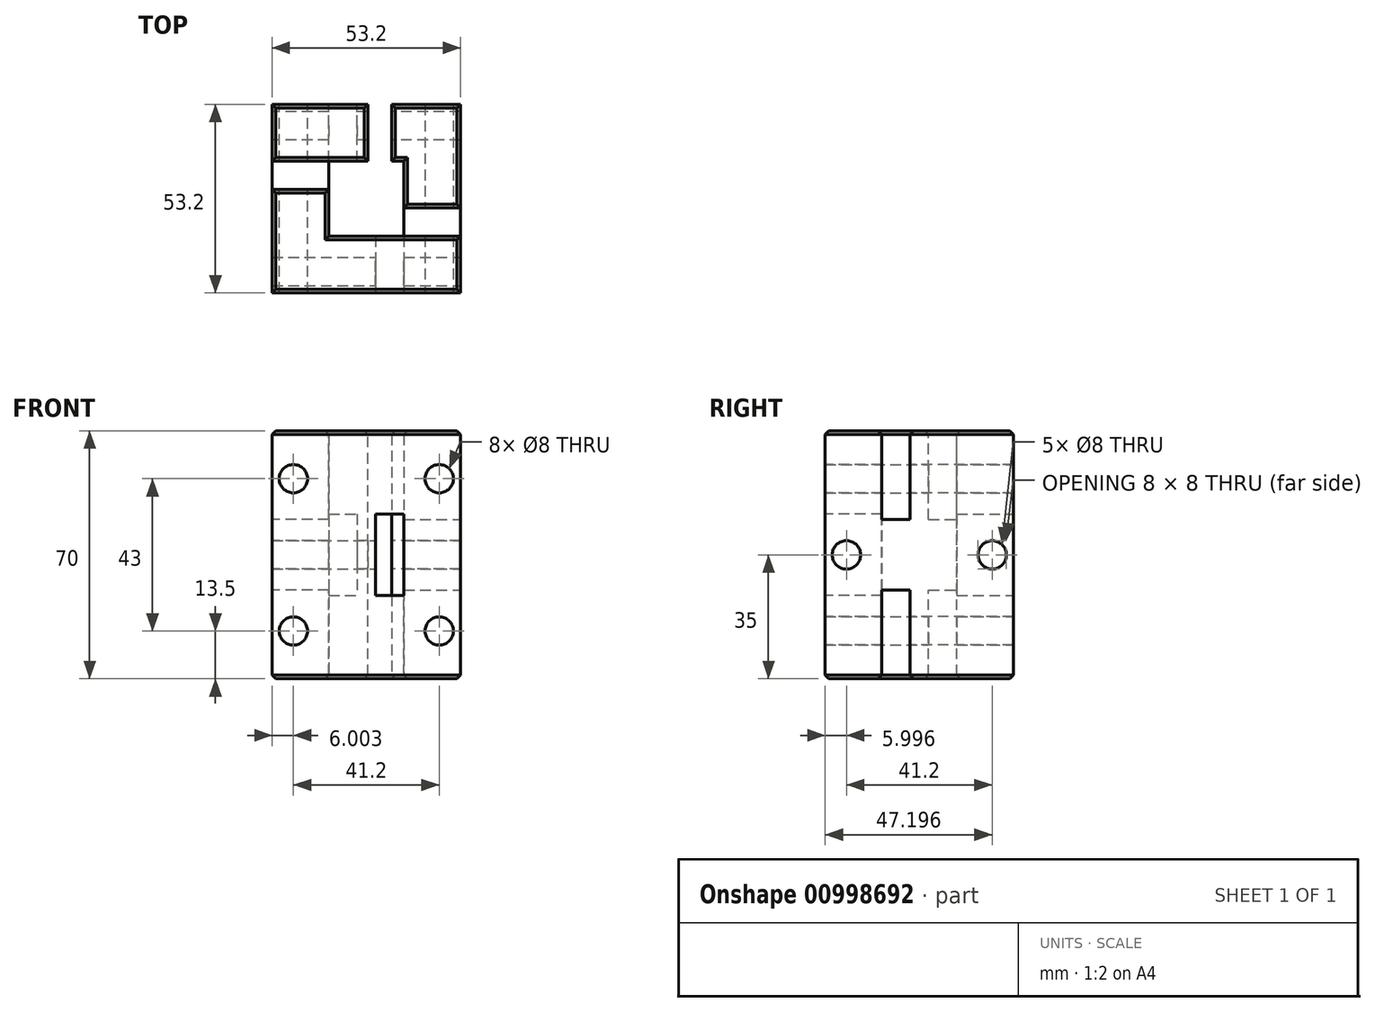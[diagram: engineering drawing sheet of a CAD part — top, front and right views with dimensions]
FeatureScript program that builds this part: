
annotation { "Feature Type Name" : "Feature", "Feature Type Description" : "" }
export const myFeature = defineFeature(function(context is Context, id is Id, definition is map)
    precondition{}
    {
        {
            var Q0;
            Q0=qCreatedBy(makeId("Top.planeOp"),FACE);
            var sketch = newSketch(context, id + "F0", { "sketchPlane" : qUnion([Q0])});
            skLineSegment(sketch, "E0.bottom", {"start": v(-39.95, 37.27) * mm, "end": v(-18.75, 37.27) * mm});
            skLineSegment(sketch, "E0.top", {"start": v(-39.95, 16.07) * mm, "end": v(-18.75, 16.07) * mm});
            skLineSegment(sketch, "E0.left", {"start": v(-39.95, 37.27) * mm, "end": v(-39.95, 16.07) * mm});
            skLineSegment(sketch, "E0.right", {"start": v(-18.75, 37.27) * mm, "end": v(-18.75, 16.07) * mm});
            skLineSegment(sketch, "E1.0", {"start": v(-55.95, 53.27) * mm, "end": v(-2.75, 53.27) * mm});
            skLineSegment(sketch, "E1.1", {"start": v(-55.95, 53.27) * mm, "end": v(-55.95, 0.07) * mm});
            skLineSegment(sketch, "E1.2", {"start": v(-55.95, 0.07) * mm, "end": v(-2.75, 0.07) * mm});
            skLineSegment(sketch, "E1.3", {"start": v(-2.75, 53.27) * mm, "end": v(-2.75, 0.07) * mm});
            skSolve(sketch);
        }
        {
            var Q0;
            Q0=makeQuery(id+"F0.imprint","IMPRINT",FACE,{"disambiguationData":[TD([[makeQuery(id+"F0.imprint","IMPRINT",EDGE,{"derivedFrom":sQuery(id+"F0.wireOp",EDGE,"E0.bottom")}),1.0]])]});
            extrude(context, id + "F1", {"entities" : qUnion([Q0]), "depth" : 70 * mm, "offsetDistance" : 25 * mm});
        }
        {
            var Q0;
            Q0=makeQuery(id+"F1.opExtrude","SWEPT_FACE",FACE,{"disambiguationData":[OSD([sQuery(id+"F0.wireOp",EDGE,"E1.1")])]});
            var sketch = newSketch(context, id + "F2", { "sketchPlane" : qUnion([Q0])});
            skLineSegment(sketch, "E2.bottom", {"start": v(-53.27, 0) * mm, "end": v(-37.27, 0) * mm});
            skLineSegment(sketch, "E2.top", {"start": v(-53.27, 70) * mm, "end": v(-37.27, 70) * mm});
            skLineSegment(sketch, "E2.left", {"start": v(-53.27, 0) * mm, "end": v(-53.27, 70) * mm});
            skLineSegment(sketch, "E2.right", {"start": v(-37.27, 0) * mm, "end": v(-37.27, 70) * mm});
            skLineSegment(sketch, "E3.bottom", {"start": v(-37.27, 2) * mm, "end": v(-29.27, 2) * mm});
            skLineSegment(sketch, "E3.top", {"start": v(-37.27, 25) * mm, "end": v(-29.27, 25) * mm});
            skLineSegment(sketch, "E3.left", {"start": v(-37.27, 2) * mm, "end": v(-37.27, 25) * mm});
            skLineSegment(sketch, "E3.right", {"start": v(-29.27, 2) * mm, "end": v(-29.27, 25) * mm});
            skLineSegment(sketch, "E4.bottom", {"start": v(-37.27, 68) * mm, "end": v(-29.27, 68) * mm});
            skLineSegment(sketch, "E4.top", {"start": v(-37.27, 45) * mm, "end": v(-29.27, 45) * mm});
            skLineSegment(sketch, "E4.left", {"start": v(-37.27, 68) * mm, "end": v(-37.27, 45) * mm});
            skLineSegment(sketch, "E4.right", {"start": v(-29.27, 68) * mm, "end": v(-29.27, 45) * mm});
            skPoint(sketch, "E5.centerSnap0", {"position": v(-53.27, 35) * mm});
            skPoint(sketch, "E6.oppositeSnap0", {"position": v(-26.67, 0) * mm});
            skLineSegment(sketch, "E6.top", {"start": v(-37.27, 0) * mm, "end": v(-29.27, 0) * mm});
            skLineSegment(sketch, "E6.left", {"start": v(-37.27, 2) * mm, "end": v(-37.27, 0) * mm});
            skLineSegment(sketch, "E6.right", {"start": v(-29.27, 2) * mm, "end": v(-29.27, 0) * mm});
            skLineSegment(sketch, "E7.bottom", {"start": v(-29.27, 68) * mm, "end": v(-37.27, 68) * mm});
            skLineSegment(sketch, "E7.top", {"start": v(-29.27, 70) * mm, "end": v(-37.27, 70) * mm});
            skLineSegment(sketch, "E7.left", {"start": v(-29.27, 68) * mm, "end": v(-29.27, 70) * mm});
            skLineSegment(sketch, "E7.right", {"start": v(-37.27, 68) * mm, "end": v(-37.27, 70) * mm});
            skCircle(sketch, "E8", {"center": v(-47.27, 35) * mm, "radius": 4 * mm});
            skLineSegment(sketch, "E9.bottom", {"start": v(-29.27, 17.5) * mm, "end": v(-37.27, 17.5) * mm});
            skLineSegment(sketch, "E9.top", {"start": v(-29.27, 9.5) * mm, "end": v(-37.27, 9.5) * mm});
            skLineSegment(sketch, "E9.left", {"start": v(-29.27, 17.5) * mm, "end": v(-29.27, 9.5) * mm});
            skLineSegment(sketch, "E9.right", {"start": v(-37.27, 17.5) * mm, "end": v(-37.27, 9.5) * mm});
            skPoint(sketch, "E9.middle", {"position": v(-33.27, 13.5) * mm});
            skPoint(sketch, "E9.middle.positionSnap0", {"position": v(-33.27, 25) * mm});
            skPoint(sketch, "E9.middle.positionSnap1", {"position": v(-37.27, 13.5) * mm});
            skPoint(sketch, "E9.centerSnap0", {"position": v(-33.27, 25) * mm});
            skPoint(sketch, "E9.centerSnap1", {"position": v(-37.27, 13.5) * mm});
            skLineSegment(sketch, "E10.bottom", {"start": v(-29.27, 17.5) * mm, "end": v(-53.27, 17.5) * mm});
            skLineSegment(sketch, "E10.top", {"start": v(-29.27, 9.5) * mm, "end": v(-53.27, 9.5) * mm});
            skLineSegment(sketch, "E10.right", {"start": v(-53.27, 17.5) * mm, "end": v(-53.27, 9.5) * mm});
            skLineSegment(sketch, "E11.bottom", {"start": v(-29.27, 60.5) * mm, "end": v(-37.27, 60.5) * mm});
            skLineSegment(sketch, "E11.top", {"start": v(-29.27, 52.5) * mm, "end": v(-37.27, 52.5) * mm});
            skLineSegment(sketch, "E11.left", {"start": v(-29.27, 60.5) * mm, "end": v(-29.27, 52.5) * mm});
            skLineSegment(sketch, "E11.right", {"start": v(-37.27, 60.5) * mm, "end": v(-37.27, 52.5) * mm});
            skPoint(sketch, "E11.middle", {"position": v(-33.27, 56.5) * mm});
            skPoint(sketch, "E11.middle.positionSnap0", {"position": v(-33.27, 45) * mm});
            skPoint(sketch, "E11.middle.positionSnap1", {"position": v(-37.27, 56.5) * mm});
            skPoint(sketch, "E11.centerSnap0", {"position": v(-33.27, 45) * mm});
            skPoint(sketch, "E11.centerSnap1", {"position": v(-37.27, 56.5) * mm});
            skLineSegment(sketch, "E12.bottom", {"start": v(-29.27, 52.5) * mm, "end": v(-53.27, 52.5) * mm});
            skLineSegment(sketch, "E12.top", {"start": v(-29.27, 60.5) * mm, "end": v(-53.27, 60.5) * mm});
            skLineSegment(sketch, "E12.left", {"start": v(-29.27, 52.5) * mm, "end": v(-29.27, 60.5) * mm});
            skLineSegment(sketch, "E12.right", {"start": v(-53.27, 52.5) * mm, "end": v(-53.27, 60.5) * mm});
            skSolve(sketch);
        }
        {
            var Q0;
            Q0=makeQuery(id+"F1.opExtrude","SWEPT_FACE",FACE,{"disambiguationData":[OSD([sQuery(id+"F0.wireOp",EDGE,"E1.0")])]});
            var sketch = newSketch(context, id + "F3", { "sketchPlane" : qUnion([Q0])});
            skLineSegment(sketch, "E13.bottom", {"start": v(55.95, 70) * mm, "end": v(39.95, 70) * mm});
            skLineSegment(sketch, "E13.top", {"start": v(55.95, 0) * mm, "end": v(39.95, 0) * mm});
            skLineSegment(sketch, "E13.left", {"start": v(55.95, 70) * mm, "end": v(55.95, 0) * mm});
            skLineSegment(sketch, "E13.right", {"start": v(39.95, 70) * mm, "end": v(39.95, 0) * mm});
            skLineSegment(sketch, "E14.bottom", {"start": v(39.95, 46.5) * mm, "end": v(31.95, 46.5) * mm});
            skLineSegment(sketch, "E14.top", {"start": v(39.95, 23.5) * mm, "end": v(31.95, 23.5) * mm});
            skLineSegment(sketch, "E14.left", {"start": v(39.95, 46.5) * mm, "end": v(39.95, 23.5) * mm});
            skLineSegment(sketch, "E14.right", {"start": v(31.95, 46.5) * mm, "end": v(31.95, 23.5) * mm});
            skPoint(sketch, "E15", {"position": v(39.95, 35) * mm});
            skCircle(sketch, "E16", {"center": v(49.95, 56.5) * mm, "radius": 4 * mm});
            skCircle(sketch, "E17", {"center": v(49.95, 13.5) * mm, "radius": 4 * mm});
            skSolve(sketch);
        }
        {
            var Q0;
            {var subQ0=sQuery(id+"F2.wireOp",EDGE,"E4.top");Q0=makeQuery(id+"F2.imprint","IMPRINT",FACE,{"disambiguationData":[TD([[makeQuery(id+"F2.imprint","IMPRINT",EDGE,{"derivedFrom":subQ0}),1.0]])]});}
            var Q1;
            {var subQ0=sQuery(id+"F2.wireOp",EDGE,"E11.bottom");Q1=makeQuery(id+"F2.imprint","IMPRINT",FACE,{"disambiguationData":[TD([[makeQuery(id+"F2.imprint","IMPRINT",EDGE,{"derivedFrom":subQ0}),1.0]])]});}
            var Q2;
            {var subQ0=sQuery(id+"F2.wireOp",EDGE,"E4.bottom");Q2=makeQuery(id+"F2.imprint","IMPRINT",FACE,{"disambiguationData":[TD([[makeQuery(id+"F2.imprint","IMPRINT",EDGE,{"derivedFrom":subQ0}),-1.0]])]});}
            var Q3;
            {var subQ2=sQuery(id+"F2.wireOp",EDGE,"E4.bottom");Q3=makeQuery(id+"F2.imprint","IMPRINT",FACE,{"disambiguationData":[TD([[makeQuery(id+"F2.imprint","IMPRINT",EDGE,{"derivedFrom":subQ2}),1.0]])]});}
            var Q4;
            {var subQ2=sQuery(id+"F2.wireOp",EDGE,"E3.bottom");Q4=makeQuery(id+"F2.imprint","IMPRINT",FACE,{"disambiguationData":[TD([[makeQuery(id+"F2.imprint","IMPRINT",EDGE,{"derivedFrom":subQ2}),-1.0]])]});}
            var Q5;
            {var subQ0=sQuery(id+"F2.wireOp",EDGE,"E3.bottom");Q5=makeQuery(id+"F2.imprint","IMPRINT",FACE,{"disambiguationData":[TD([[makeQuery(id+"F2.imprint","IMPRINT",EDGE,{"derivedFrom":subQ0}),1.0]])]});}
            var Q6;
            {var subQ0=sQuery(id+"F2.wireOp",EDGE,"E9.bottom");Q6=makeQuery(id+"F2.imprint","IMPRINT",FACE,{"disambiguationData":[TD([[makeQuery(id+"F2.imprint","IMPRINT",EDGE,{"derivedFrom":subQ0}),1.0]])]});}
            var Q7;
            {var subQ0=sQuery(id+"F2.wireOp",EDGE,"E3.top");Q7=makeQuery(id+"F2.imprint","IMPRINT",FACE,{"disambiguationData":[TD([[makeQuery(id+"F2.imprint","IMPRINT",EDGE,{"derivedFrom":subQ0}),-1.0]])]});}
            extrude(context, id + "F4", {"entities" : qUnion([Q0, Q1, Q2, Q3, Q4, Q5, Q6, Q7]), "operationType" : NewBodyOperationType.REMOVE, "oppositeDirection" : true, "depth" : 24 * mm, "offsetDistance" : 25 * mm});
        }
        {
            var Q0;
            {var subQ2=sQuery(id+"F3.wireOp",EDGE,"E14.bottom");Q0=makeQuery(id+"F3.imprint","IMPRINT",FACE,{"disambiguationData":[TD([[makeQuery(id+"F3.imprint","IMPRINT",EDGE,{"derivedFrom":subQ2}),1.0]])]});}
            extrude(context, id + "F5", {"entities" : qUnion([Q0]), "operationType" : NewBodyOperationType.REMOVE, "oppositeDirection" : true, "depth" : 25 * mm, "offsetDistance" : 25 * mm});
        }
        {
            var Q0;
            Q0=makeQuery(id+"F2.imprint","IMPRINT",FACE,{"disambiguationData":[TD([[makeQuery(id+"F2.imprint","IMPRINT",EDGE,{"derivedFrom":sQuery(id+"F2.wireOp",EDGE,"E8")}),1.0]])]});
            extrude(context, id + "F6", {"entities" : qUnion([Q0]), "operationType" : NewBodyOperationType.REMOVE, "oppositeDirection" : true, "depth" : 90 * mm, "offsetDistance" : 25 * mm});
        }
        {
            var Q0;
            Q0=makeQuery(id+"F1.opExtrude","SWEPT_FACE",FACE,{"disambiguationData":[OSD([sQuery(id+"F0.wireOp",EDGE,"E1.3")])]});
            var sketch = newSketch(context, id + "F7", { "sketchPlane" : qUnion([Q0])});
            skLineSegment(sketch, "E18.bottom", {"start": v(0.07, 0) * mm, "end": v(16.07, 0) * mm});
            skLineSegment(sketch, "E18.top", {"start": v(0.07, 70) * mm, "end": v(16.07, 70) * mm});
            skLineSegment(sketch, "E18.left", {"start": v(0.07, 0) * mm, "end": v(0.07, 70) * mm});
            skLineSegment(sketch, "E18.right", {"start": v(16.07, 0) * mm, "end": v(16.07, 70) * mm});
            skLineSegment(sketch, "E19.bottom", {"start": v(16.07, 2) * mm, "end": v(24.07, 2) * mm});
            skLineSegment(sketch, "E19.top", {"start": v(16.07, 25) * mm, "end": v(24.07, 25) * mm});
            skLineSegment(sketch, "E19.left", {"start": v(16.07, 2) * mm, "end": v(16.07, 25) * mm});
            skLineSegment(sketch, "E19.right", {"start": v(24.07, 2) * mm, "end": v(24.07, 25) * mm});
            skLineSegment(sketch, "E20.bottom", {"start": v(16.07, 68) * mm, "end": v(24.07, 68) * mm});
            skLineSegment(sketch, "E20.top", {"start": v(16.07, 45) * mm, "end": v(24.07, 45) * mm});
            skLineSegment(sketch, "E20.left", {"start": v(16.07, 68) * mm, "end": v(16.07, 45) * mm});
            skLineSegment(sketch, "E20.right", {"start": v(24.07, 68) * mm, "end": v(24.07, 45) * mm});
            skLineSegment(sketch, "E21.bottom", {"start": v(24.07, 68) * mm, "end": v(16.07, 68) * mm});
            skLineSegment(sketch, "E21.top", {"start": v(24.07, 70) * mm, "end": v(16.07, 70) * mm});
            skLineSegment(sketch, "E21.left", {"start": v(24.07, 68) * mm, "end": v(24.07, 70) * mm});
            skLineSegment(sketch, "E21.right", {"start": v(16.07, 68) * mm, "end": v(16.07, 70) * mm});
            skLineSegment(sketch, "E22.bottom", {"start": v(24.07, 2) * mm, "end": v(16.07, 2) * mm});
            skLineSegment(sketch, "E22.top", {"start": v(24.07, 0) * mm, "end": v(16.07, 0) * mm});
            skLineSegment(sketch, "E22.left", {"start": v(24.07, 2) * mm, "end": v(24.07, 0) * mm});
            skLineSegment(sketch, "E22.right", {"start": v(16.07, 2) * mm, "end": v(16.07, 0) * mm});
            skCircle(sketch, "E23", {"center": v(6.07, 35) * mm, "radius": 4 * mm});
            skPoint(sketch, "E23.centerSnap0", {"position": v(0.07, 35) * mm});
            skLineSegment(sketch, "E24.bottom", {"start": v(24.07, 17.5) * mm, "end": v(16.07, 17.5) * mm});
            skLineSegment(sketch, "E24.top", {"start": v(24.07, 9.5) * mm, "end": v(16.07, 9.5) * mm});
            skLineSegment(sketch, "E24.left", {"start": v(24.07, 17.5) * mm, "end": v(24.07, 9.5) * mm});
            skLineSegment(sketch, "E24.right", {"start": v(16.07, 17.5) * mm, "end": v(16.07, 9.5) * mm});
            skPoint(sketch, "E24.middle", {"position": v(20.07, 13.5) * mm});
            skPoint(sketch, "E24.middle.positionSnap0", {"position": v(16.07, 13.5) * mm});
            skPoint(sketch, "E24.middle.positionSnap1", {"position": v(20.07, 25) * mm});
            skPoint(sketch, "E24.centerSnap0", {"position": v(16.07, 13.5) * mm});
            skPoint(sketch, "E24.centerSnap1", {"position": v(20.07, 25) * mm});
            skLineSegment(sketch, "E25.bottom", {"start": v(24.07, 60.5) * mm, "end": v(16.07, 60.5) * mm});
            skLineSegment(sketch, "E25.top", {"start": v(24.07, 52.5) * mm, "end": v(16.07, 52.5) * mm});
            skLineSegment(sketch, "E25.left", {"start": v(24.07, 60.5) * mm, "end": v(24.07, 52.5) * mm});
            skLineSegment(sketch, "E25.right", {"start": v(16.07, 60.5) * mm, "end": v(16.07, 52.5) * mm});
            skPoint(sketch, "E25.middle", {"position": v(20.07, 56.5) * mm});
            skPoint(sketch, "E25.middle.positionSnap0", {"position": v(16.07, 56.5) * mm});
            skPoint(sketch, "E25.middle.positionSnap1", {"position": v(20.07, 45) * mm});
            skPoint(sketch, "E25.centerSnap0", {"position": v(16.07, 56.5) * mm});
            skPoint(sketch, "E25.centerSnap1", {"position": v(20.07, 45) * mm});
            skLineSegment(sketch, "E26.bottom", {"start": v(24.07, 52.5) * mm, "end": v(0.07, 52.5) * mm});
            skLineSegment(sketch, "E26.top", {"start": v(24.07, 60.5) * mm, "end": v(0.07, 60.5) * mm});
            skLineSegment(sketch, "E26.left", {"start": v(24.07, 52.5) * mm, "end": v(24.07, 60.5) * mm});
            skLineSegment(sketch, "E26.right", {"start": v(0.07, 52.5) * mm, "end": v(0.07, 60.5) * mm});
            skLineSegment(sketch, "E27.bottom", {"start": v(24.07, 9.5) * mm, "end": v(0.07, 9.5) * mm});
            skLineSegment(sketch, "E27.top", {"start": v(24.07, 17.5) * mm, "end": v(0.07, 17.5) * mm});
            skLineSegment(sketch, "E27.left", {"start": v(24.07, 9.5) * mm, "end": v(24.07, 17.5) * mm});
            skLineSegment(sketch, "E27.right", {"start": v(0.07, 9.5) * mm, "end": v(0.07, 17.5) * mm});
            skSolve(sketch);
        }
        {
            var Q0;
            {var subQ0=sQuery(id+"F7.wireOp",EDGE,"E20.top");Q0=makeQuery(id+"F7.imprint","IMPRINT",FACE,{"disambiguationData":[TD([[makeQuery(id+"F7.imprint","IMPRINT",EDGE,{"derivedFrom":subQ0}),1.0]])]});}
            var Q1;
            {var subQ2=sQuery(id+"F7.wireOp",EDGE,"E20.bottom");Q1=makeQuery(id+"F7.imprint","IMPRINT",FACE,{"disambiguationData":[TD([[makeQuery(id+"F7.imprint","IMPRINT",EDGE,{"derivedFrom":subQ2}),1.0]])]});}
            var Q2;
            {var subQ0=sQuery(id+"F7.wireOp",EDGE,"E19.top");Q2=makeQuery(id+"F7.imprint","IMPRINT",FACE,{"disambiguationData":[TD([[makeQuery(id+"F7.imprint","IMPRINT",EDGE,{"derivedFrom":subQ0}),-1.0]])]});}
            var Q3;
            {var subQ2=sQuery(id+"F7.wireOp",EDGE,"E19.bottom");Q3=makeQuery(id+"F7.imprint","IMPRINT",FACE,{"disambiguationData":[TD([[makeQuery(id+"F7.imprint","IMPRINT",EDGE,{"derivedFrom":subQ2}),-1.0]])]});}
            var Q4;
            {var subQ0=sQuery(id+"F7.wireOp",EDGE,"E25.bottom");Q4=makeQuery(id+"F7.imprint","IMPRINT",FACE,{"disambiguationData":[TD([[makeQuery(id+"F7.imprint","IMPRINT",EDGE,{"derivedFrom":subQ0}),1.0]])]});}
            var Q5;
            {var subQ0=sQuery(id+"F7.wireOp",EDGE,"E20.bottom");Q5=makeQuery(id+"F7.imprint","IMPRINT",FACE,{"disambiguationData":[TD([[makeQuery(id+"F7.imprint","IMPRINT",EDGE,{"derivedFrom":subQ0}),-1.0]])]});}
            var Q6;
            {var subQ0=sQuery(id+"F7.wireOp",EDGE,"E24.bottom");Q6=makeQuery(id+"F7.imprint","IMPRINT",FACE,{"disambiguationData":[TD([[makeQuery(id+"F7.imprint","IMPRINT",EDGE,{"derivedFrom":subQ0}),1.0]])]});}
            var Q7;
            {var subQ0=sQuery(id+"F7.wireOp",EDGE,"E19.bottom");Q7=makeQuery(id+"F7.imprint","IMPRINT",FACE,{"disambiguationData":[TD([[makeQuery(id+"F7.imprint","IMPRINT",EDGE,{"derivedFrom":subQ0}),1.0]])]});}
            extrude(context, id + "F8", {"entities" : qUnion([Q0, Q1, Q2, Q3, Q4, Q5, Q6, Q7]), "operationType" : NewBodyOperationType.REMOVE, "oppositeDirection" : true, "depth" : 25 * mm, "offsetDistance" : 25 * mm});
        }
        {
            var Q0;
            Q0=makeQuery(id+"F3.imprint","IMPRINT",FACE,{"disambiguationData":[TD([[makeQuery(id+"F3.imprint","IMPRINT",EDGE,{"derivedFrom":sQuery(id+"F3.wireOp",EDGE,"E16")}),1.0]])]});
            var Q1;
            Q1=makeQuery(id+"F3.imprint","IMPRINT",FACE,{"disambiguationData":[TD([[makeQuery(id+"F3.imprint","IMPRINT",EDGE,{"derivedFrom":sQuery(id+"F3.wireOp",EDGE,"E17")}),1.0]])]});
            extrude(context, id + "F9", {"entities" : qUnion([Q0, Q1]), "operationType" : NewBodyOperationType.REMOVE, "oppositeDirection" : true, "depth" : 100 * mm, "offsetDistance" : 25 * mm});
        }
        {
            var Q0;
            Q0=makeQuery(id+"F7.imprint","IMPRINT",FACE,{"disambiguationData":[TD([[makeQuery(id+"F7.imprint","IMPRINT",EDGE,{"derivedFrom":sQuery(id+"F7.wireOp",EDGE,"E23")}),1.0]])]});
            extrude(context, id + "F10", {"entities" : qUnion([Q0]), "operationType" : NewBodyOperationType.REMOVE, "oppositeDirection" : true, "depth" : 90 * mm, "offsetDistance" : 25 * mm});
        }
        {
            var Q0;
            Q0=makeQuery(id+"F1.opExtrude","SWEPT_FACE",FACE,{"disambiguationData":[OSD([sQuery(id+"F0.wireOp",EDGE,"E1.2")])]});
            var sketch = newSketch(context, id + "F11", { "sketchPlane" : qUnion([Q0])});
            skLineSegment(sketch, "E28.bottom", {"start": v(-2.75, 70) * mm, "end": v(-18.75, 70) * mm});
            skLineSegment(sketch, "E28.top", {"start": v(-2.75, 0) * mm, "end": v(-18.75, 0) * mm});
            skLineSegment(sketch, "E28.left", {"start": v(-2.75, 70) * mm, "end": v(-2.75, 0) * mm});
            skLineSegment(sketch, "E28.right", {"start": v(-18.75, 70) * mm, "end": v(-18.75, 0) * mm});
            skLineSegment(sketch, "E29.bottom", {"start": v(-18.75, 46.5) * mm, "end": v(-26.75, 46.5) * mm});
            skLineSegment(sketch, "E29.top", {"start": v(-18.75, 23.5) * mm, "end": v(-26.75, 23.5) * mm});
            skLineSegment(sketch, "E29.left", {"start": v(-18.75, 46.5) * mm, "end": v(-18.75, 23.5) * mm});
            skLineSegment(sketch, "E29.right", {"start": v(-26.75, 46.5) * mm, "end": v(-26.75, 23.5) * mm});
            skPoint(sketch, "E30", {"position": v(-18.75, 35) * mm});
            skCircle(sketch, "E31", {"center": v(-8.75, 56.5) * mm, "radius": 4 * mm});
            skCircle(sketch, "E32", {"center": v(-8.75, 13.5) * mm, "radius": 4 * mm});
            skSolve(sketch);
        }
        {
            var Q0;
            {var subQ2=sQuery(id+"F11.wireOp",EDGE,"E29.bottom");Q0=makeQuery(id+"F11.imprint","IMPRINT",FACE,{"disambiguationData":[TD([[makeQuery(id+"F11.imprint","IMPRINT",EDGE,{"derivedFrom":subQ2}),1.0]])]});}
            extrude(context, id + "F12", {"entities" : qUnion([Q0]), "operationType" : NewBodyOperationType.REMOVE, "oppositeDirection" : true, "depth" : 25 * mm, "offsetDistance" : 25 * mm});
        }
        {
            var Q0;
            Q0=makeQuery(id+"F11.imprint","IMPRINT",FACE,{"disambiguationData":[TD([[makeQuery(id+"F11.imprint","IMPRINT",EDGE,{"derivedFrom":sQuery(id+"F11.wireOp",EDGE,"E32")}),1.0]])]});
            var Q1;
            Q1=makeQuery(id+"F11.imprint","IMPRINT",FACE,{"disambiguationData":[TD([[makeQuery(id+"F11.imprint","IMPRINT",EDGE,{"derivedFrom":sQuery(id+"F11.wireOp",EDGE,"E31")}),1.0]])]});
            extrude(context, id + "F13", {"entities" : qUnion([Q0, Q1]), "operationType" : NewBodyOperationType.REMOVE, "oppositeDirection" : true, "depth" : 90 * mm, "offsetDistance" : 25 * mm});
        }
        {
            var Q0;
            Q0=makeQuery(id+"F1.opExtrude","SWEPT_FACE",FACE,{"disambiguationData":[OSD([sQuery(id+"F0.wireOp",EDGE,"E1.0")])]});
            var sketch = newSketch(context, id + "F14", { "sketchPlane" : qUnion([Q0])});
            skLineSegment(sketch, "E33", {"start": v(1.95, 70) * mm, "end": v(15.45, 70) * mm});
            skLineSegment(sketch, "E34", {"start": v(28.95, 70) * mm, "end": v(42.45, 70) * mm});
            skLineSegment(sketch, "E35", {"start": v(15.45, 70) * mm, "end": v(28.95, 70) * mm});
            skLineSegment(sketch, "E36", {"start": v(42.45, 70) * mm, "end": v(55.95, 70) * mm});
            skLineSegment(sketch, "E37", {"start": v(1.95, 70) * mm, "end": v(1.95, 52.5) * mm});
            skLineSegment(sketch, "E38", {"start": v(1.95, 0) * mm, "end": v(15.45, 0) * mm});
            skLineSegment(sketch, "E39", {"start": v(28.95, 0) * mm, "end": v(42.45, 0) * mm});
            skLineSegment(sketch, "E40", {"start": v(15.45, 0) * mm, "end": v(28.95, 0) * mm});
            skLineSegment(sketch, "E41", {"start": v(42.45, 0) * mm, "end": v(55.95, 0) * mm});
            skLineSegment(sketch, "E42", {"start": v(1.95, 35) * mm, "end": v(1.95, 17.5) * mm});
            skLineSegment(sketch, "E43", {"start": v(1.95, 52.5) * mm, "end": v(1.95, 35) * mm});
            skLineSegment(sketch, "E44", {"start": v(1.95, 17.5) * mm, "end": v(1.95, 0) * mm});
            skLineSegment(sketch, "E45", {"start": v(1.95, 52.5) * mm, "end": v(55.95, 52.5) * mm});
            skLineSegment(sketch, "E46", {"start": v(55.95, 52.5) * mm, "end": v(55.95, 17.5) * mm});
            skLineSegment(sketch, "E47", {"start": v(55.95, 17.5) * mm, "end": v(1.95, 17.5) * mm});
            skPoint(sketch, "E48.endSnap0", {"position": v(22.2, 70) * mm});
            skLineSegment(sketch, "E49", {"start": v(28.95, 70) * mm, "end": v(22.2, 52.5) * mm});
            skLineSegment(sketch, "E50", {"start": v(22.2, 52.5) * mm, "end": v(22.2, 70) * mm});
            skLineSegment(sketch, "E51", {"start": v(28.95, 0) * mm, "end": v(22.2, 17.5) * mm});
            skPoint(sketch, "E51.endSnap0", {"position": v(22.2, 0) * mm});
            skLineSegment(sketch, "E52", {"start": v(22.2, 17.5) * mm, "end": v(22.2, 0) * mm});
            skPoint(sketch, "E53.startSnap0", {"position": v(25.57, 61.25) * mm});
            skLineSegment(sketch, "E54", {"start": v(22.2, 47) * mm, "end": v(28.95, 61.25) * mm});
            skPoint(sketch, "E55.startSnap0", {"position": v(22.2, 8.75) * mm});
            skLineSegment(sketch, "E56", {"start": v(22.2, 23) * mm, "end": v(28.95, 8.75) * mm});
            skLineSegment(sketch, "E57", {"start": v(28.95, 8.75) * mm, "end": v(28.95, 61.25) * mm});
            skPoint(sketch, "E58.endSnap0", {"position": v(28.95, 35) * mm});
            skPoint(sketch, "E59", {"position": v(22.2, 24.5) * mm});
            skPoint(sketch, "E60", {"position": v(22.2, 45.5) * mm});
            skPoint(sketch, "E61", {"position": v(27.45, 35) * mm});
            skLineSegment(sketch, "E62", {"start": v(27.45, 35) * mm, "end": v(22.2, 45.5) * mm});
            skLineSegment(sketch, "E63", {"start": v(22.2, 24.5) * mm, "end": v(27.45, 35) * mm});
            skLineSegment(sketch, "E64", {"start": v(22.2, 45.5) * mm, "end": v(22.2, 24.5) * mm});
            skLineSegment(sketch, "E65", {"start": v(28.95, 33.5) * mm, "end": v(28.95, 36.5) * mm});
            skLineSegment(sketch, "E66", {"start": v(28.95, 36.5) * mm, "end": v(22.2, 47) * mm});
            skLineSegment(sketch, "E67", {"start": v(28.95, 33.5) * mm, "end": v(22.2, 23) * mm});
            skLineSegment(sketch, "E68", {"start": v(28.95, 70) * mm, "end": v(28.95, 0) * mm});
            skLineSegment(sketch, "E69", {"start": v(22.2, 0) * mm, "end": v(22.2, 70) * mm});
            skSolve(sketch);
        }
        {
            var Q0;
            {var subQ0=sQuery(id+"F14.wireOp",EDGE,"E51");Q0=makeQuery(id+"F14.imprint","IMPRINT",FACE,{"disambiguationData":[TD([[makeQuery(id+"F14.imprint","IMPRINT",EDGE,{"derivedFrom":subQ0}),1.0]])]});}
            var Q1;
            Q1=makeQuery(id+"F14.imprint","IMPRINT",FACE,{"disambiguationData":[TD([[makeQuery(id+"F14.imprint","IMPRINT",EDGE,{"derivedFrom":sQuery(id+"F14.wireOp",EDGE,"E62")}),1.0]])]});
            var Q2;
            {var subQ0=sQuery(id+"F14.wireOp",EDGE,"E56");var subQ1=sQuery(id+"F14.wireOp",EDGE,"E47");var subQ2=makeQuery(id+"F14.imprint","INTERSECT",VERTEX,{"derivedFrom":[subQ1,subQ0]});Q2=makeQuery(id+"F14.imprint","IMPRINT",FACE,{"disambiguationData":[TD([[makeQuery(id+"F14.imprint","IMPRINT",EDGE,{"disambiguationData":[TD([[subQ2,1.0]])],"derivedFrom":subQ1}),1.0]])]});}
            var Q3;
            {var subQ0=sQuery(id+"F14.wireOp",EDGE,"E57");var subQ1=sQuery(id+"F14.wireOp",EDGE,"E45");var subQ2=makeQuery(id+"F14.imprint","INTERSECT",VERTEX,{"derivedFrom":[subQ1,subQ0]});Q3=makeQuery(id+"F14.imprint","IMPRINT",FACE,{"disambiguationData":[TD([[makeQuery(id+"F14.imprint","IMPRINT",EDGE,{"disambiguationData":[TD([[subQ2,1.0]])],"derivedFrom":subQ1}),1.0]])]});}
            var Q4;
            {var subQ0=sQuery(id+"F14.wireOp",EDGE,"E58");Q4=makeQuery(id+"F14.imprint","IMPRINT",FACE,{"disambiguationData":[TD([[makeQuery(id+"F14.imprint","IMPRINT",EDGE,{"derivedFrom":subQ0}),1.0]])]});}
            var Q5;
            {var subQ5=sQuery(id+"F14.wireOp",EDGE,"E67");Q5=makeQuery(id+"F14.imprint","IMPRINT",FACE,{"disambiguationData":[TD([[makeQuery(id+"F14.imprint","IMPRINT",EDGE,{"derivedFrom":subQ5}),1.0]])]});}
            var Q6;
            {var subQ5=sQuery(id+"F14.wireOp",EDGE,"E66");Q6=makeQuery(id+"F14.imprint","IMPRINT",FACE,{"disambiguationData":[TD([[makeQuery(id+"F14.imprint","IMPRINT",EDGE,{"derivedFrom":subQ5}),-1.0]])]});}
            var Q7;
            {var subQ2=sQuery(id+"F14.wireOp",EDGE,"E62");Q7=makeQuery(id+"F14.imprint","IMPRINT",FACE,{"disambiguationData":[TD([[makeQuery(id+"F14.imprint","IMPRINT",EDGE,{"derivedFrom":subQ2}),-1.0]])]});}
            var Q8;
            {var subQ0=sQuery(id+"F14.wireOp",EDGE,"E51");Q8=makeQuery(id+"F14.imprint","IMPRINT",FACE,{"disambiguationData":[TD([[makeQuery(id+"F14.imprint","IMPRINT",EDGE,{"derivedFrom":subQ0}),-1.0]])]});}
            var Q9;
            {var subQ1=sQuery(id+"F14.wireOp",EDGE,"E45");var subQ3=sQuery(id+"F14.wireOp",EDGE,"E54");var subQ4=makeQuery(id+"F14.imprint","INTERSECT",VERTEX,{"derivedFrom":[subQ1,subQ3]});Q9=makeQuery(id+"F14.imprint","IMPRINT",FACE,{"disambiguationData":[TD([[makeQuery(id+"F14.imprint","IMPRINT",EDGE,{"disambiguationData":[TD([[subQ4,1.0]])],"derivedFrom":subQ3}),1.0]])]});}
            var Q10;
            {var subQ1=sQuery(id+"F14.wireOp",EDGE,"E47");var subQ3=sQuery(id+"F14.wireOp",EDGE,"E56");var subQ4=makeQuery(id+"F14.imprint","INTERSECT",VERTEX,{"derivedFrom":[subQ1,subQ3]});Q10=makeQuery(id+"F14.imprint","IMPRINT",FACE,{"disambiguationData":[TD([[makeQuery(id+"F14.imprint","IMPRINT",EDGE,{"disambiguationData":[TD([[subQ4,1.0]])],"derivedFrom":subQ3}),-1.0]])]});}
            var Q11;
            {var subQ0=sQuery(id+"F14.wireOp",EDGE,"E49");Q11=makeQuery(id+"F14.imprint","IMPRINT",FACE,{"disambiguationData":[TD([[makeQuery(id+"F14.imprint","IMPRINT",EDGE,{"derivedFrom":subQ0}),-1.0]])]});}
            var Q12;
            {var subQ0=sQuery(id+"F14.wireOp",EDGE,"E49");Q12=makeQuery(id+"F14.imprint","IMPRINT",FACE,{"disambiguationData":[TD([[makeQuery(id+"F14.imprint","IMPRINT",EDGE,{"derivedFrom":subQ0}),1.0]])]});}
            extrude(context, id + "F15", {"entities" : qUnion([Q0, Q1, Q2, Q3, Q4, Q5, Q6, Q7, Q8, Q9, Q10, Q11, Q12]), "operationType" : NewBodyOperationType.REMOVE, "oppositeDirection" : true, "depth" : 25 * mm, "offsetDistance" : 25 * mm});
        }
        {
            var Q0;
            {var subQ0=sQuery(id+"F0.wireOp",EDGE,"E0.bottom");var subQ1=makeQuery(id+"F1.opExtrude","SWEPT_FACE",FACE,{"disambiguationData":[OSD([subQ0])]});var subQ2=sQuery(id+"F0.wireOp",EDGE,"E1.0");var subQ4=sQuery(id+"F0.wireOp",EDGE,"E1.1");var subQ5=makeQuery(id+"F1.opExtrude","SWEPT_FACE",FACE,{"disambiguationData":[OSD([subQ4])]});var subQ6=sQuery(id+"F0.wireOp",EDGE,"E0.right");var subQ7=sQuery(id+"F0.wireOp",EDGE,"E1.3");Q0=makeQuery(id+"F15.boolean.opBoolean","SPLIT",FACE,{"disambiguationData":[TD([subQ5])],"derivedFrom":makeQuery(id+"F8.boolean.opBoolean","SPLIT",FACE,{"disambiguationData":[TD([subQ1])],"derivedFrom":makeQuery(id+"F1.opExtrude","CAP_FACE",FACE,{"disambiguationData":[OSD([subQ0,sQuery(id+"F0.wireOp",EDGE,"E0.top"),sQuery(id+"F0.wireOp",EDGE,"E0.left"),subQ6,subQ2,subQ4,sQuery(id+"F0.wireOp",EDGE,"E1.2"),subQ7])],"isStart":true})})});}
            var Q1;
            {var subQ0=sQuery(id+"F0.wireOp",EDGE,"E1.3");var subQ2=sQuery(id+"F0.wireOp",EDGE,"E1.0");var subQ4=sQuery(id+"F0.wireOp",EDGE,"E0.right");var subQ5=makeQuery(id+"F1.opExtrude","SWEPT_FACE",FACE,{"disambiguationData":[OSD([subQ4])]});var subQ6=sQuery(id+"F0.wireOp",EDGE,"E0.bottom");var subQ7=makeQuery(id+"F1.opExtrude","SWEPT_FACE",FACE,{"disambiguationData":[OSD([subQ6])]});var subQ9=sQuery(id+"F0.wireOp",EDGE,"E1.1");Q1=makeQuery(id+"F15.boolean.opBoolean","SPLIT",FACE,{"disambiguationData":[TD([subQ5])],"derivedFrom":makeQuery(id+"F8.boolean.opBoolean","SPLIT",FACE,{"disambiguationData":[TD([subQ7])],"derivedFrom":makeQuery(id+"F1.opExtrude","CAP_FACE",FACE,{"disambiguationData":[OSD([subQ6,sQuery(id+"F0.wireOp",EDGE,"E0.top"),sQuery(id+"F0.wireOp",EDGE,"E0.left"),subQ4,subQ2,subQ9,sQuery(id+"F0.wireOp",EDGE,"E1.2"),subQ0])],"isStart":true})})});}
            var Q2;
            {var subQ0=sQuery(id+"F0.wireOp",EDGE,"E1.1");var subQ1=sQuery(id+"F0.wireOp",EDGE,"E0.left");var subQ2=sQuery(id+"F0.wireOp",EDGE,"E1.2");var subQ3=sQuery(id+"F0.wireOp",EDGE,"E0.top");var subQ4=sQuery(id+"F0.wireOp",EDGE,"E1.3");Q2=makeQuery(id+"F8.boolean.opBoolean","SPLIT",FACE,{"disambiguationData":[TD([makeQuery(id+"F1.opExtrude","SWEPT_FACE",FACE,{"disambiguationData":[OSD([subQ3])]})])],"derivedFrom":makeQuery(id+"F1.opExtrude","CAP_FACE",FACE,{"disambiguationData":[OSD([sQuery(id+"F0.wireOp",EDGE,"E0.bottom"),subQ3,subQ1,sQuery(id+"F0.wireOp",EDGE,"E0.right"),sQuery(id+"F0.wireOp",EDGE,"E1.0"),subQ0,subQ2,subQ4])],"isStart":true})});}
            var Q3;
            {var subQ0=sQuery(id+"F0.wireOp",EDGE,"E0.bottom");var subQ1=makeQuery(id+"F1.opExtrude","SWEPT_FACE",FACE,{"disambiguationData":[OSD([subQ0])]});var subQ2=sQuery(id+"F0.wireOp",EDGE,"E1.0");var subQ4=sQuery(id+"F0.wireOp",EDGE,"E1.1");var subQ5=makeQuery(id+"F1.opExtrude","SWEPT_FACE",FACE,{"disambiguationData":[OSD([subQ4])]});var subQ6=sQuery(id+"F0.wireOp",EDGE,"E0.right");var subQ7=sQuery(id+"F0.wireOp",EDGE,"E1.3");Q3=makeQuery(id+"F15.boolean.opBoolean","SPLIT",FACE,{"disambiguationData":[TD([subQ5])],"derivedFrom":makeQuery(id+"F8.boolean.opBoolean","SPLIT",FACE,{"disambiguationData":[TD([subQ1])],"derivedFrom":makeQuery(id+"F1.opExtrude","CAP_FACE",FACE,{"disambiguationData":[OSD([subQ0,sQuery(id+"F0.wireOp",EDGE,"E0.top"),sQuery(id+"F0.wireOp",EDGE,"E0.left"),subQ6,subQ2,subQ4,sQuery(id+"F0.wireOp",EDGE,"E1.2"),subQ7])],"isStart":false})})});}
            var Q4;
            {var subQ0=sQuery(id+"F0.wireOp",EDGE,"E1.1");var subQ1=sQuery(id+"F0.wireOp",EDGE,"E0.left");var subQ2=sQuery(id+"F0.wireOp",EDGE,"E1.2");var subQ3=sQuery(id+"F0.wireOp",EDGE,"E0.top");var subQ4=sQuery(id+"F0.wireOp",EDGE,"E1.3");Q4=makeQuery(id+"F8.boolean.opBoolean","SPLIT",FACE,{"disambiguationData":[TD([makeQuery(id+"F1.opExtrude","SWEPT_FACE",FACE,{"disambiguationData":[OSD([subQ3])]})])],"derivedFrom":makeQuery(id+"F1.opExtrude","CAP_FACE",FACE,{"disambiguationData":[OSD([sQuery(id+"F0.wireOp",EDGE,"E0.bottom"),subQ3,subQ1,sQuery(id+"F0.wireOp",EDGE,"E0.right"),sQuery(id+"F0.wireOp",EDGE,"E1.0"),subQ0,subQ2,subQ4])],"isStart":false})});}
            var Q5;
            {var subQ0=sQuery(id+"F0.wireOp",EDGE,"E1.3");var subQ2=sQuery(id+"F0.wireOp",EDGE,"E1.0");var subQ4=sQuery(id+"F0.wireOp",EDGE,"E0.right");var subQ5=makeQuery(id+"F1.opExtrude","SWEPT_FACE",FACE,{"disambiguationData":[OSD([subQ4])]});var subQ6=sQuery(id+"F0.wireOp",EDGE,"E0.bottom");var subQ7=makeQuery(id+"F1.opExtrude","SWEPT_FACE",FACE,{"disambiguationData":[OSD([subQ6])]});var subQ9=sQuery(id+"F0.wireOp",EDGE,"E1.1");Q5=makeQuery(id+"F15.boolean.opBoolean","SPLIT",FACE,{"disambiguationData":[TD([subQ5])],"derivedFrom":makeQuery(id+"F8.boolean.opBoolean","SPLIT",FACE,{"disambiguationData":[TD([subQ7])],"derivedFrom":makeQuery(id+"F1.opExtrude","CAP_FACE",FACE,{"disambiguationData":[OSD([subQ6,sQuery(id+"F0.wireOp",EDGE,"E0.top"),sQuery(id+"F0.wireOp",EDGE,"E0.left"),subQ4,subQ2,subQ9,sQuery(id+"F0.wireOp",EDGE,"E1.2"),subQ0])],"isStart":false})})});}
            chamfer(context, id + "F16", {"entities" : qUnion([Q0, Q1, Q2, Q3, Q4, Q5]), "width" : 1 * mm, "tangentPropagation" : true});
        }
    });
